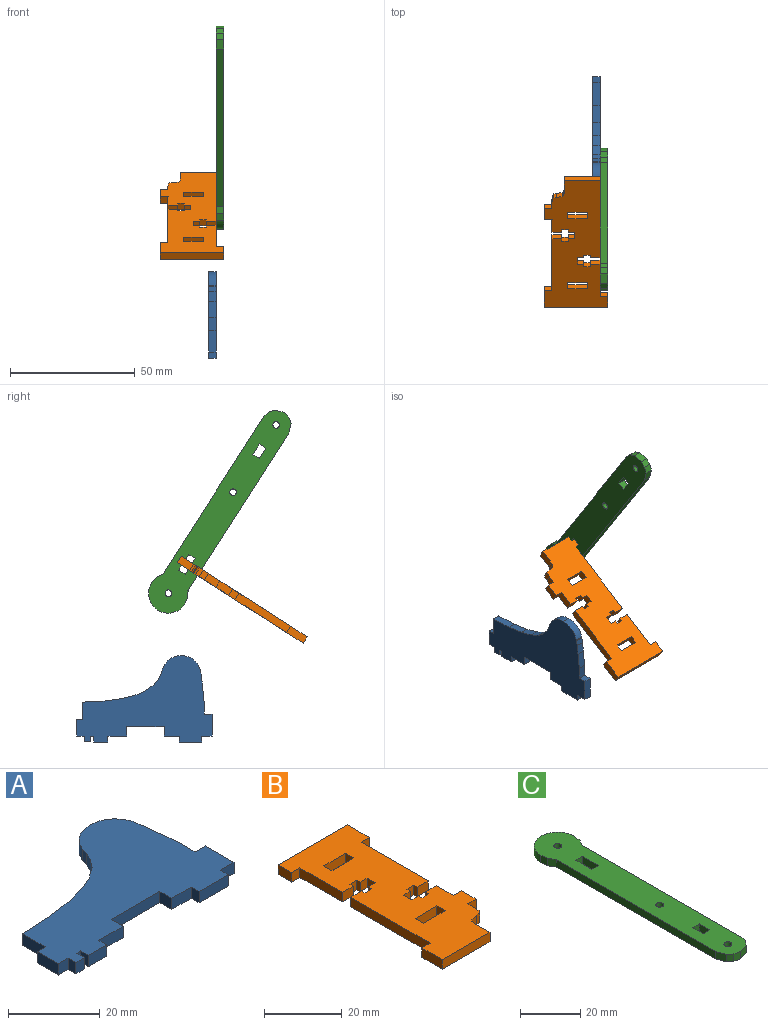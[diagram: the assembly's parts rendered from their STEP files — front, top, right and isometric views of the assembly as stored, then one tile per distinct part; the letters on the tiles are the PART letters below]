
ASSEMBLY  parts=3 mates=1
PART A: 47 faces, bbox 54.2x34.6x3 mm
  f0: plane 3x0mm, normal (-0.98,0.18,0), area 0mm2, adj f1,f44,f45,f46
  f1: cylinder r=7.83mm len=7.53mm, axis (0,0,-1), area 29.9mm2, adj f0,f2,f45,f46
  f2: cylinder r=7.9mm len=7.49mm, axis (0,0,-1), area 29.5mm2, adj f1,f3,f45,f46
  f3: plane 3x1.68mm, normal (-0.95,0.32,0), area 5.3mm2, adj f2,f4,f45,f46
  f4: plane 3x2.18mm, normal (-0.91,0.41,0), area 7.2mm2, adj f3,f5,f45,f46
  f5: plane 3x2.43mm, normal (-0.79,0.62,0), area 9.2mm2, adj f4,f6,f45,f46
  f6: plane 3.32x3mm, normal (-0.59,0.81,0), area 12.3mm2, adj f5,f7,f45,f46
  f7: plane 3.93x3mm, normal (-0.4,0.92,0), area 12.9mm2, adj f6,f8,f45,f46
  f8: plane 5.36x3mm, normal (-0.26,0.97,0), area 16.6mm2, adj f7,f9,f45,f46
  f9: plane 7.03x3mm, normal (-0.14,0.99,0), area 21.3mm2, adj f8,f10,f45,f46
  f10: plane 8.95x3mm, normal (-0.05,1,0), area 26.9mm2, adj f9,f11,f45,f46
  f11: plane 3x0.1mm, normal (0,-1,0), area 0.3mm2, adj f10,f12,f45,f46
  f12: plane 7.07x3mm, normal (-1,0,0), area 21.2mm2, adj f11,f13,f45,f46
  f13: plane 3x2.5mm, normal (0,1,0), area 7.5mm2, adj f12,f14,f45,f46
  f14: plane 6.5x3mm, normal (-1,0,0), area 19.5mm2, adj f13,f15,f45,f46
  f15: plane 3.02x3mm, normal (0,-1,0), area 9.1mm2, adj f14,f16,f45,f46
  f16: plane 3x2.25mm, normal (-1,0,0), area 6.7mm2, adj f15,f17,f45,f46
  f17: plane 3x0.15mm, normal (-1,0,0), area 0.4mm2, adj f16,f18,f45,f46
  f18: plane 3x2.7mm, normal (0,-1,0), area 8.1mm2, adj f17,f19,f45,f46
  f19: plane 3x2.4mm, normal (1,0,0), area 7.2mm2, adj f18,f20,f45,f46
  f20: cylinder r=397.55mm len=3mm, axis (0,0,-1), area 3.5mm2, adj f19,f21,f45,f46
  f21: plane 3x2.4mm, normal (-1,0,0), area 7.2mm2, adj f20,f22,f45,f46
  f22: plane 5.62x3mm, normal (0,-1,0), area 16.9mm2, adj f21,f23,f45,f46
  f23: plane 3x2.4mm, normal (1,0,0), area 7.2mm2, adj f22,f24,f45,f46
  f24: plane 7.48x3mm, normal (0,-1,0), area 22.4mm2, adj f23,f25,f45,f46
  f25: plane 3.7x3mm, normal (1,0,0), area 11.1mm2, adj f24,f26,f45,f46
  f26: plane 15x3mm, normal (0,-1,0), area 45mm2, adj f25,f27,f45,f46
  f27: plane 3.7x3mm, normal (-1,0,0), area 11.1mm2, adj f26,f28,f45,f46
  f28: plane 6.04x3mm, normal (0,-1,0), area 18.1mm2, adj f27,f29,f45,f46
  f29: plane 3x2.4mm, normal (-1,0,0), area 7.2mm2, adj f28,f30,f45,f46
  f30: plane 9x3mm, normal (0,-1,0), area 27mm2, adj f29,f31,f45,f46
  f31: plane 3x2.4mm, normal (1,0,0), area 7.2mm2, adj f30,f32,f45,f46
  f32: plane 4.16x3mm, normal (0,-1,0), area 12.5mm2, adj f31,f33,f45,f46
  f33: plane 8.8x3mm, normal (1,0,0), area 26.4mm2, adj f32,f34,f45,f46
  f34: plane 3.2x3mm, normal (0,1,0), area 9.6mm2, adj f33,f35,f45,f46
  f35: plane 4.9x3mm, normal (1,0,0), area 14.7mm2, adj f34,f36,f45,f46
  f36: plane 6.6x3mm, normal (1,0.1,0), area 19.9mm2, adj f35,f37,f45,f46
  f37: plane 3.99x3mm, normal (0.99,0.12,0), area 12.1mm2, adj f36,f38,f45,f46
  f38: plane 3x1.96mm, normal (0.99,0.16,0), area 5.9mm2, adj f37,f39,f45,f46
  f39: plane 3x0.47mm, normal (0.97,0.22,0), area 1.4mm2, adj f38,f40,f45,f46
  f40: plane 3x0.01mm, normal (0.93,0.37,0), area 0mm2, adj f39,f41,f45,f46
  f41: plane 3x0mm, normal (0.87,0.5,0), area 0mm2, adj f40,f42,f45,f46
  f42: plane 3x0mm, normal (0.65,0.76,0), area 0mm2, adj f41,f43,f45,f46
  f43: plane 3x0mm, normal (0.09,1,0), area 0mm2, adj f42,f44,f45,f46
  f44: plane 3x0mm, normal (-0.81,0.58,0), area 0mm2, adj f0,f43,f45,f46
  f45: plane 54.2x34.6mm, normal (0,0,1), area 1045.2mm2, adj f0,f1,f2,f3,f4,f5,f6,f7
  f46: plane 54.2x34.6mm, normal (0,0,-1), area 1045.2mm2, adj f0,f1,f2,f3,f4,f5,f6,f7
PART B: 57 faces, bbox 25.3x60x3 mm
  f0: plane 3x3mm, normal (1,0,0), area 9mm2, adj f1,f54,f55,f56
  f1: plane 8x3mm, normal (0,-1,0), area 24mm2, adj f0,f2,f55,f56
  f2: plane 3x3mm, normal (-1,0,0), area 9mm2, adj f1,f54,f55,f56
  f3: plane 3x3mm, normal (1,0,0), area 9mm2, adj f4,f52,f55,f56
  f4: plane 8x3mm, normal (0,-1,0), area 24mm2, adj f3,f5,f55,f56
  f5: plane 3x3mm, normal (-1,0,0), area 9mm2, adj f4,f52,f55,f56
  f6: plane 3x2.45mm, normal (1,0.01,0), area 7.3mm2, adj f7,f53,f55,f56
  f7: plane 3.02x3mm, normal (0,-1,0), area 9.1mm2, adj f6,f8,f55,f56
  f8: plane 5.37x3mm, normal (1,0,0), area 16.1mm2, adj f7,f9,f55,f56
  f9: plane 3x0.04mm, normal (0,1,0), area 0.1mm2, adj f8,f10,f55,f56
  f10: plane 3x3mm, normal (0,1,0), area 9mm2, adj f9,f11,f55,f56
  f11: plane 3x0.04mm, normal (0,-1,0), area 0.1mm2, adj f10,f12,f55,f56
  f12: plane 6.13x3mm, normal (1,0,0), area 18.4mm2, adj f11,f13,f55,f56
  f13: plane 4x3mm, normal (0,1,0), area 12mm2, adj f12,f14,f55,f56
  f14: plane 3x1.25mm, normal (-1,0,0), area 3.8mm2, adj f13,f15,f55,f56
  f15: plane 3x2.5mm, normal (0,1,0), area 7.5mm2, adj f14,f16,f55,f56
  f16: plane 3x1.25mm, normal (1,0,0), area 3.8mm2, adj f15,f17,f55,f56
  f17: plane 3x2.5mm, normal (0,1,0), area 7.5mm2, adj f16,f18,f55,f56
  f18: plane 3x3mm, normal (1,0,0), area 9mm2, adj f17,f19,f55,f56
  f19: plane 3x2.5mm, normal (0,-1,0), area 7.5mm2, adj f18,f20,f55,f56
  f20: plane 3x1.25mm, normal (1,0,0), area 3.8mm2, adj f19,f21,f55,f56
  f21: plane 3x2.5mm, normal (0,-1,0), area 7.5mm2, adj f20,f22,f55,f56
  f22: plane 3x1.25mm, normal (-1,0,0), area 3.8mm2, adj f21,f23,f55,f56
  f23: plane 4x3mm, normal (0,-1,0), area 12mm2, adj f22,f24,f55,f56
  f24: plane 24.5x3mm, normal (1,0,0), area 73.5mm2, adj f23,f25,f55,f56
  f25: plane 3x3mm, normal (0,-1,0), area 9mm2, adj f24,f26,f55,f56
  f26: plane 8x3mm, normal (1,0,0), area 24mm2, adj f25,f27,f55,f56
  f27: plane 25.3x3mm, normal (0,1,0), area 75.9mm2, adj f26,f28,f55,f56
  f28: plane 5x3mm, normal (-1,0,0), area 15mm2, adj f27,f29,f55,f56
  f29: plane 3x3mm, normal (0,-1,0), area 9mm2, adj f28,f30,f55,f56
  f30: plane 15.5x3mm, normal (-1,0,0), area 46.5mm2, adj f29,f31,f55,f56
  f31: plane 4x3mm, normal (0,-1,0), area 12mm2, adj f30,f32,f55,f56
  f32: plane 3x1.25mm, normal (1,0,0), area 3.8mm2, adj f31,f33,f55,f56
  f33: plane 3x2.5mm, normal (0,-1,0), area 7.5mm2, adj f32,f34,f55,f56
  f34: plane 3x1.25mm, normal (-1,0,0), area 3.8mm2, adj f33,f35,f55,f56
  f35: plane 3x2.5mm, normal (0,-1,0), area 7.5mm2, adj f34,f36,f55,f56
  f36: plane 3x3mm, normal (-1,0,0), area 9mm2, adj f35,f37,f55,f56
  f37: plane 3x2.5mm, normal (0,1,0), area 7.5mm2, adj f36,f38,f55,f56
  f38: plane 3x1.25mm, normal (-1,0,0), area 3.8mm2, adj f37,f39,f55,f56
  f39: plane 3x2.5mm, normal (0,1,0), area 7.5mm2, adj f38,f40,f55,f56
  f40: plane 3x1.25mm, normal (1,0,0), area 3.8mm2, adj f39,f41,f55,f56
  f41: plane 4x3mm, normal (0,1,0), area 12mm2, adj f40,f42,f55,f56
  f42: plane 29x3mm, normal (-1,0,0), area 87mm2, adj f41,f43,f55,f56
  f43: plane 3x3mm, normal (0,1,0), area 9mm2, adj f42,f44,f55,f56
  f44: plane 7.5x3mm, normal (-1,0,0), area 22.5mm2, adj f43,f45,f55,f56
  f45: plane 17.37x3mm, normal (0,-1,0), area 52.1mm2, adj f44,f46,f55,f56
  f46: plane 5.88x3mm, normal (1,0,0), area 17.6mm2, adj f45,f47,f55,f56
  f47: plane 3x1mm, normal (0.97,-0.23,0), area 3.1mm2, adj f46,f48,f55,f56
  f48: plane 3x0.65mm, normal (0.67,-0.74,0), area 2.6mm2, adj f47,f49,f55,f56
  f49: plane 3x2.13mm, normal (0.18,-0.98,0), area 6.5mm2, adj f48,f50,f55,f56
  f50: plane 3x1.19mm, normal (0.17,-0.99,0), area 3.6mm2, adj f49,f51,f55,f56
  f51: plane 3x0.71mm, normal (0.78,-0.62,0), area 2.7mm2, adj f50,f53,f55,f56
  f52: plane 8x3mm, normal (0,1,0), area 24mm2, adj f3,f5,f55,f56
  f53: plane 3x1.8mm, normal (1,-0.09,0), area 5.4mm2, adj f6,f51,f55,f56
  f54: plane 8x3mm, normal (0,1,0), area 24mm2, adj f0,f2,f55,f56
  f55: plane 60x25.3mm, normal (0,0,1), area 1082.9mm2, adj f0,f1,f2,f3,f4,f5,f6,f7
  f56: plane 60x25.3mm, normal (0,0,-1), area 1082.9mm2, adj f0,f1,f2,f3,f4,f5,f6,f7
PART C: 29 faces, bbox 15.8x94x3 mm
  f0: plane 3x2.59mm, normal (-0.87,-0.5,0), area 9mm2, adj f1,f22,f27,f28
  f1: plane 3x0.04mm, normal (0.99,-0.11,0), area 0.1mm2, adj f0,f2,f27,f28
  f2: plane 74.86x3mm, normal (-1,0,0), area 224.6mm2, adj f1,f3,f27,f28
  f3: plane 3.83x3mm, normal (-0.94,-0.34,0), area 12.2mm2, adj f2,f4,f27,f28
  f4: plane 3x2.02mm, normal (-0.62,-0.79,0), area 7.7mm2, adj f3,f5,f27,f28
  f5: plane 3x2.59mm, normal (-0.22,-0.98,0), area 8mm2, adj f4,f6,f27,f28
  f6: plane 3.83x3mm, normal (0.33,-0.94,0), area 12.2mm2, adj f5,f7,f27,f28
  f7: plane 3x1.99mm, normal (0.78,-0.62,0), area 7.6mm2, adj f6,f8,f27,f28
  f8: plane 3x2.58mm, normal (0.98,-0.22,0), area 7.9mm2, adj f7,f9,f27,f28
  f9: plane 74.93x3mm, normal (1,0,0), area 224.8mm2, adj f8,f10,f27,f28
  f10: plane 3x0.06mm, normal (-0.86,-0.5,0), area 0.2mm2, adj f9,f11,f27,f28
  f11: plane 3x1.96mm, normal (0.84,-0.54,0), area 7mm2, adj f10,f12,f27,f28
  f12: plane 3.31x3mm, normal (0.98,-0.19,0), area 10.1mm2, adj f11,f13,f27,f28
  f13: cylinder r=7.9mm len=7.9mm, axis (0,0,-1), area 37.3mm2, adj f12,f14,f27,f28
  f14: cylinder r=7.9mm len=7.9mm, axis (0,0,-1), area 37.3mm2, adj f13,f22,f27,f28
  f15: plane 3.1x3mm, normal (0,1,0), area 9.3mm2, adj f16,f23,f27,f28
  f16: plane 5x3mm, normal (1,0,0), area 15mm2, adj f15,f17,f27,f28
  f17: plane 3.1x3mm, normal (0,-1,0), area 9.3mm2, adj f16,f23,f27,f28
  f18: plane 7.5x3mm, normal (-1,0,0), area 22.5mm2, adj f19,f24,f27,f28
  f19: plane 3.1x3mm, normal (0,1,0), area 9.3mm2, adj f18,f20,f27,f28
  f20: plane 7.5x3mm, normal (1,0,0), area 22.5mm2, adj f19,f24,f27,f28
  f21: cylinder r=1.32mm len=3mm, axis (0,0,-1), area 25mm2, adj f27,f28
  f22: plane 3x2.67mm, normal (-0.99,-0.15,0), area 8.1mm2, adj f0,f14,f27,f28
  f23: plane 5x3mm, normal (-1,0,0), area 15mm2, adj f15,f17,f27,f28
  f24: plane 3.1x3mm, normal (0,-1,0), area 9.3mm2, adj f18,f20,f27,f28
  f25: cylinder r=1.32mm len=3mm, axis (0,0,-1), area 25mm2, adj f27,f28
  f26: cylinder r=1.32mm len=3mm, axis (0,0,-1), area 25mm2, adj f27,f28
  f27: plane 93.98x15.81mm, normal (0,0,1), area 1070.6mm2, adj f0,f1,f2,f3,f4,f5,f6,f7
  f28: plane 93.98x15.81mm, normal (0,0,-1), area 1070.6mm2, adj f0,f1,f2,f3,f4,f5,f6,f7
PLACE A rot(axis=(0.58,-0.58,-0.58),120deg) t=(3,-33.42,1.81)mm
PLACE B rot(axis=(0,-0.28,0.96),180deg) t=(-134.95,-31.92,43.49)mm
PLACE C rot(axis=(-0.43,-0.79,0.43),103.3deg) t=(6,-60.88,62.37)mm
MATE fastened B.f44 <-> C.f28  axis (1,0,0) through (6,-13.04,57.36)mm
